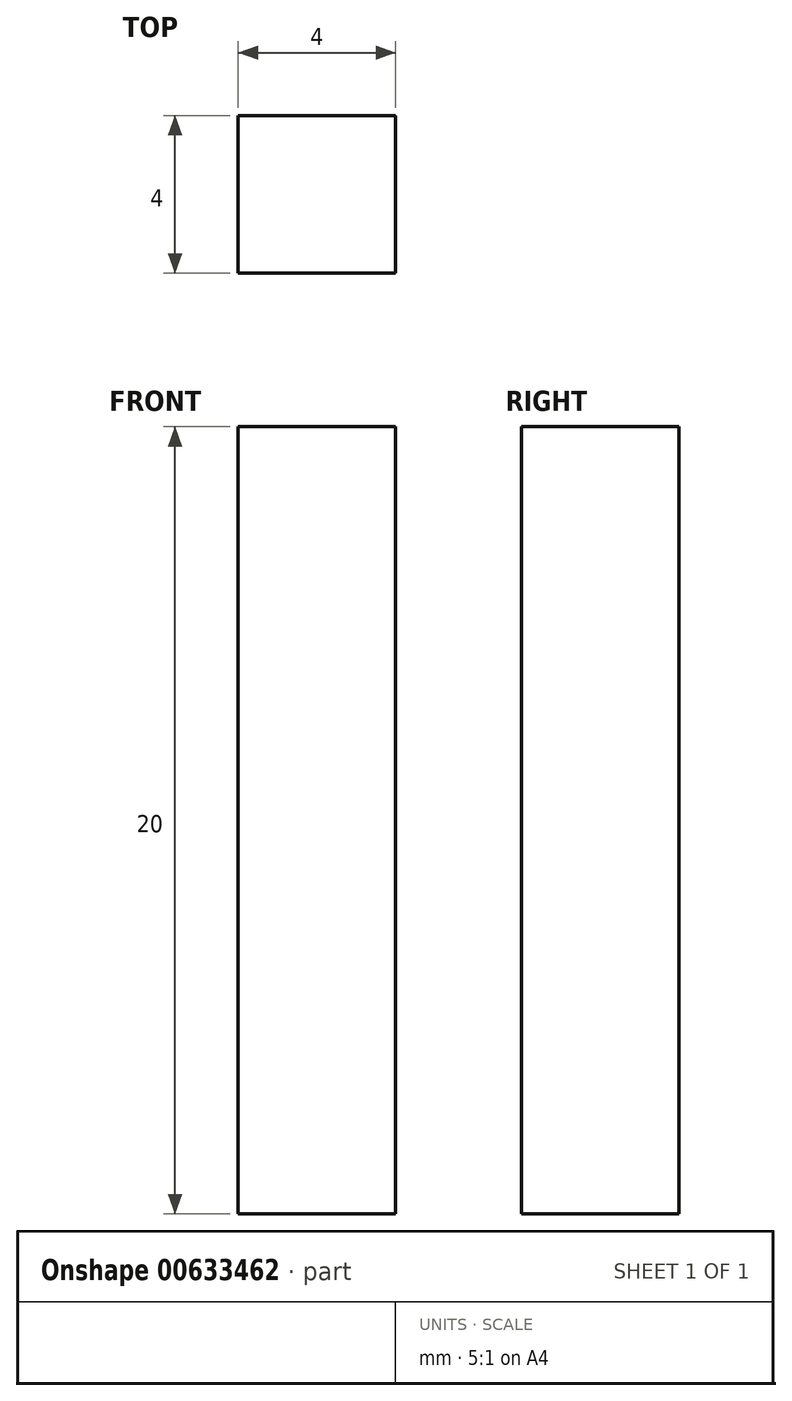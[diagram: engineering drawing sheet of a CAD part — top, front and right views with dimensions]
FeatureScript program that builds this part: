
annotation { "Feature Type Name" : "Feature", "Feature Type Description" : "" }
export const myFeature = defineFeature(function(context is Context, id is Id, definition is map)
    precondition{}
    {
        {
            var Q0;
            Q0=qCreatedBy(makeId("Right.planeOp"),FACE);
            var sketch = newSketch(context, id + "F0", { "sketchPlane" : qUnion([Q0])});
            skLineSegment(sketch, "E0.bottom", {"start": v(0, 0) * mm, "end": v(-300, 0) * mm});
            skLineSegment(sketch, "E0.left", {"start": v(0, 0) * mm, "end": v(0, 45) * mm});
            skLineSegment(sketch, "E0.right", {"start": v(-300, 0) * mm, "end": v(-300, 40) * mm});
            skLineSegment(sketch, "E1.right", {"start": v(-300, 40) * mm, "end": v(-300, 105) * mm});
            skLineSegment(sketch, "E2", {"start": v(-300, 105) * mm, "end": v(0, 45) * mm});
            skLineSegment(sketch, "E3.bottom", {"start": v(-240, 0) * mm, "end": v(-180, 0) * mm});
            skLineSegment(sketch, "E3.top", {"start": v(-240, 4) * mm, "end": v(-180, 4) * mm});
            skLineSegment(sketch, "E3.left", {"start": v(-240, 0) * mm, "end": v(-240, 4) * mm});
            skLineSegment(sketch, "E3.right", {"start": v(-180, 0) * mm, "end": v(-180, 4) * mm});
            skLineSegment(sketch, "E4.bottom", {"start": v(-120, 0) * mm, "end": v(-60, 0) * mm});
            skLineSegment(sketch, "E4.top", {"start": v(-120, 4) * mm, "end": v(-60, 4) * mm});
            skLineSegment(sketch, "E4.left", {"start": v(-120, 0) * mm, "end": v(-120, 4) * mm});
            skLineSegment(sketch, "E4.right", {"start": v(-60, 0) * mm, "end": v(-60, 4) * mm});
            skLineSegment(sketch, "E5.bottom", {"start": v(-300, 20) * mm, "end": v(-296, 20) * mm});
            skLineSegment(sketch, "E5.top", {"start": v(-300, 40) * mm, "end": v(-296, 40) * mm});
            skLineSegment(sketch, "E5.left", {"start": v(-300, 20) * mm, "end": v(-300, 40) * mm});
            skLineSegment(sketch, "E5.right", {"start": v(-296, 20) * mm, "end": v(-296, 40) * mm});
            skLineSegment(sketch, "E6.bottom", {"start": v(0, 40) * mm, "end": v(-4, 40) * mm});
            skLineSegment(sketch, "E6.top", {"start": v(0, 20) * mm, "end": v(-4, 20) * mm});
            skLineSegment(sketch, "E6.left", {"start": v(0, 40) * mm, "end": v(0, 20) * mm});
            skLineSegment(sketch, "E6.right", {"start": v(-4, 40) * mm, "end": v(-4, 20) * mm});
            skLineSegment(sketch, "E7.bottom", {"start": v(-250, 95) * mm, "end": v(-200.97, 85.2) * mm});
            skLineSegment(sketch, "E7.top", {"start": v(-250, 91) * mm, "end": v(-200.97, 81.2) * mm});
            skLineSegment(sketch, "E7.left", {"start": v(-250, 95) * mm, "end": v(-250, 91) * mm});
            skLineSegment(sketch, "E7.right", {"start": v(-200.97, 85.2) * mm, "end": v(-200.97, 81.2) * mm});
            skLineSegment(sketch, "E8.bottom", {"start": v(-150.97, 75.2) * mm, "end": v(-101.94, 65.39) * mm});
            skLineSegment(sketch, "E8.top", {"start": v(-150.97, 71.2) * mm, "end": v(-101.94, 61.39) * mm});
            skLineSegment(sketch, "E8.left", {"start": v(-150.97, 75.2) * mm, "end": v(-150.97, 71.2) * mm});
            skLineSegment(sketch, "E8.right", {"start": v(-101.94, 65.39) * mm, "end": v(-101.94, 61.39) * mm});
            skLineSegment(sketch, "E9.bottom", {"start": v(-68.2, 58.64) * mm, "end": v(-19.18, 48.84) * mm});
            skLineSegment(sketch, "E9.top", {"start": v(-68.2, 54.64) * mm, "end": v(-19.18, 44.84) * mm});
            skLineSegment(sketch, "E9.left", {"start": v(-68.2, 58.64) * mm, "end": v(-68.2, 54.64) * mm});
            skLineSegment(sketch, "E9.right", {"start": v(-19.18, 48.84) * mm, "end": v(-19.18, 44.84) * mm});
            skSolve(sketch);
        }
        {
            var Q0;
            {var subQ13=sQuery(id+"F0.wireOp",EDGE,"E0.right");Q0=makeQuery(id+"F0.imprint","IMPRINT",FACE,{"disambiguationData":[TD([[makeQuery(id+"F0.imprint","IMPRINT",EDGE,{"derivedFrom":subQ13}),-1.0]])]});}
            extrude(context, id + "F1", {"entities" : qUnion([Q0]), "depth" : 4 * mm, "offsetDistance" : 25 * mm});
        }
    });
